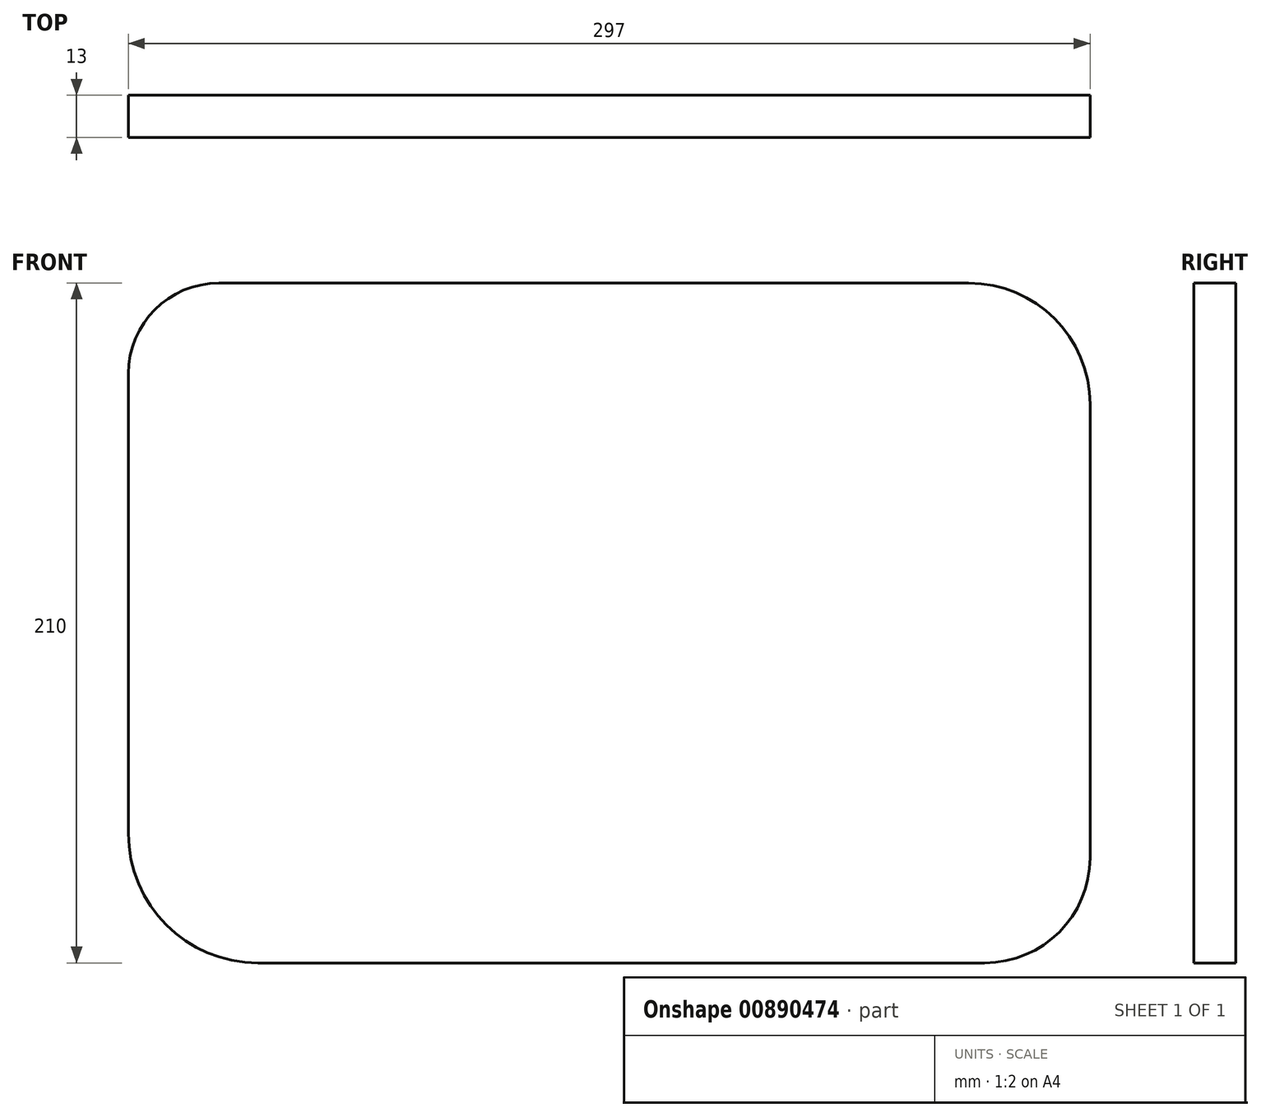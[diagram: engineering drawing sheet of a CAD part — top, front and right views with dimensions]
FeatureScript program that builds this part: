
annotation { "Feature Type Name" : "Feature", "Feature Type Description" : "" }
export const myFeature = defineFeature(function(context is Context, id is Id, definition is map)
    precondition{}
    {
        {
            var Q0;
            Q0=qCreatedBy(makeId("Front.planeOp"),FACE);
            var sketch = newSketch(context, id + "F0", { "sketchPlane" : qUnion([Q0])});
            skLineSegment(sketch, "E0.bottom", {"start": v(-120.52, 96.83) * mm, "end": v(111.02, 96.83) * mm});
            skLineSegment(sketch, "E0.top", {"start": v(-108.5, -113.17) * mm, "end": v(115.98, -113.17) * mm});
            skLineSegment(sketch, "E0.left", {"start": v(-148.5, 68.85) * mm, "end": v(-148.5, -73.17) * mm});
            skLineSegment(sketch, "E0.right", {"start": v(148.5, 59.35) * mm, "end": v(148.5, -80.65) * mm});
            skPoint(sketch, "E1.visualSharp", {"position": v(-148.5, 96.83) * mm});
            skArc(sketch, "E1.filletArc", {"start": v(-120.52, 96.83) * mm, "mid": v(-140.3, 88.63) * mm, "end": v(-148.5, 68.85) * mm});
            skPoint(sketch, "E2.visualSharp", {"position": v(148.5, 96.83) * mm});
            skArc(sketch, "E2.filletArc", {"start": v(148.5, 59.35) * mm, "mid": v(137.52, 85.85) * mm, "end": v(111.02, 96.83) * mm});
            skPoint(sketch, "E3.visualSharp", {"position": v(148.5, -113.17) * mm});
            skArc(sketch, "E3.filletArc", {"start": v(115.98, -113.17) * mm, "mid": v(138.98, -103.65) * mm, "end": v(148.5, -80.65) * mm});
            skPoint(sketch, "E4.visualSharp", {"position": v(-148.5, -113.17) * mm});
            skArc(sketch, "E4.filletArc", {"start": v(-148.5, -73.17) * mm, "mid": v(-136.78, -101.45) * mm, "end": v(-108.5, -113.17) * mm});
            skSolve(sketch);
        }
        {
            var Q0;
            Q0 = qSketchRegion(id + "F0", true);
            extrude(context, id + "F1", {"entities" : qUnion([Q0]), "depth" : 13 * mm, "offsetDistance" : 25 * mm});
        }
    });
